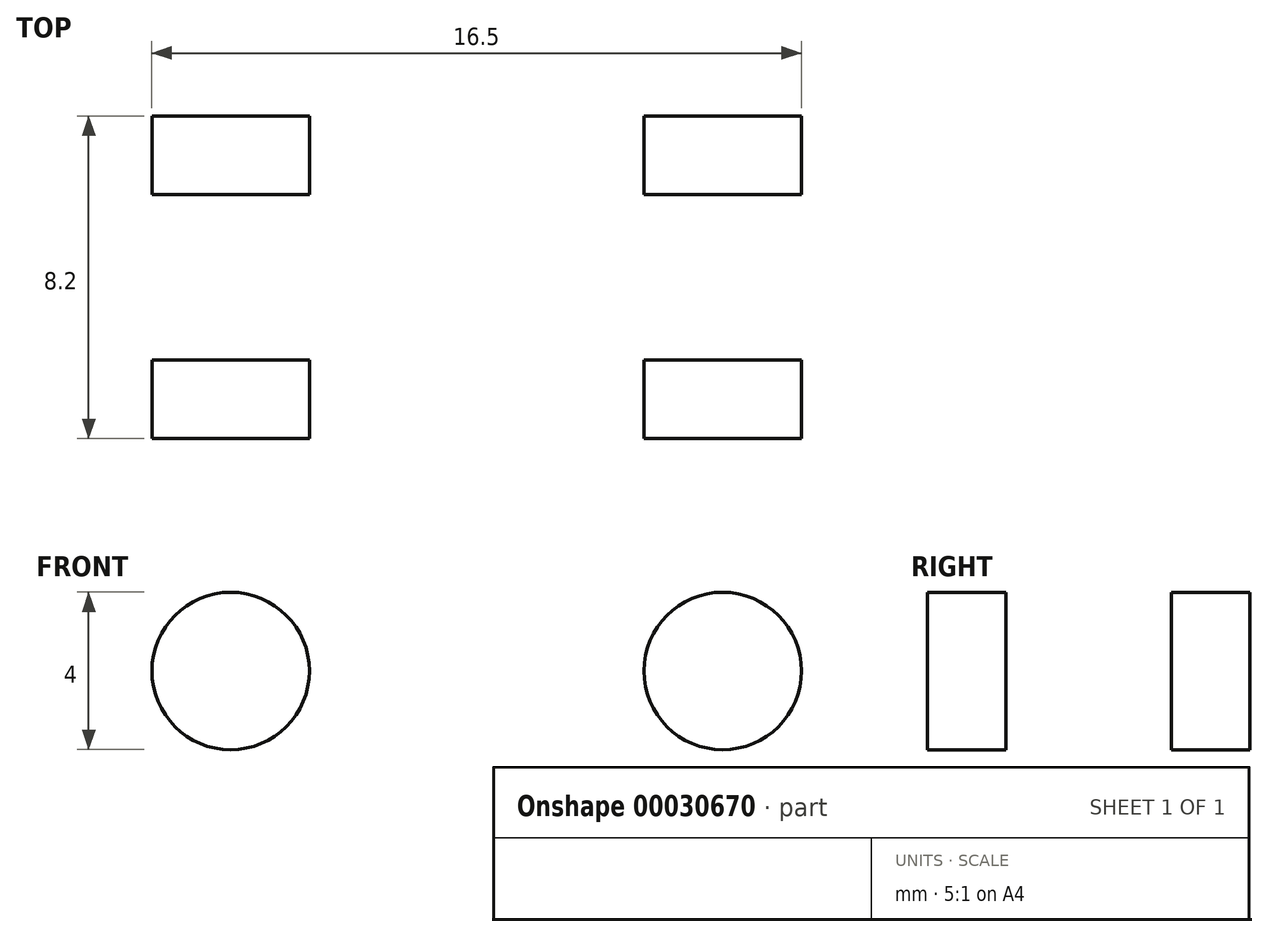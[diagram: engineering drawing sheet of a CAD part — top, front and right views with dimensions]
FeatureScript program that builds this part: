
annotation { "Feature Type Name" : "Feature", "Feature Type Description" : "" }
export const myFeature = defineFeature(function(context is Context, id is Id, definition is map)
    precondition{}
    {
        {
            var Q0;
            Q0=qCreatedBy(makeId("Front.planeOp"),FACE);
            var sketch = newSketch(context, id + "F0", { "sketchPlane" : qUnion([Q0])});
            skLineSegment(sketch, "E0", {"start": v(-39.95, 41.63) * mm, "end": v(-14.95, 41.63) * mm});
            skLineSegment(sketch, "E1", {"start": v(-39.95, 41.63) * mm, "end": v(-39.95, 11.63) * mm});
            skLineSegment(sketch, "E2", {"start": v(-39.95, 11.63) * mm, "end": v(-14.95, 11.63) * mm});
            skLineSegment(sketch, "E3", {"start": v(-14.95, 41.63) * mm, "end": v(-14.95, 11.63) * mm});
            skCircle(sketch, "E4", {"center": v(-27.45, 26.63) * mm, "radius": 2.1 * mm});
            skSolve(sketch);
        }
        {
            var Q0;
            Q0 = qSketchRegion(id + "F0", true);
            extrude(context, id + "F1", {"entities" : qUnion([Q0]), "oppositeDirection" : true, "depth" : 2 * mm});
        }
        {
            var Q0;
            Q0=makeQuery(id+"F1.opExtrude","SWEPT_FACE",FACE,{"disambiguationData":[OSD([sQuery(id+"F0.wireOp",EDGE,"E0")])]});
            var sketch = newSketch(context, id + "F2", { "sketchPlane" : qUnion([Q0])});
            skLineSegment(sketch, "E5", {"start": v(-14.95, 2) * mm, "end": v(-14.95, 6.2) * mm});
            skLineSegment(sketch, "E6", {"start": v(-14.95, 6.2) * mm, "end": v(-39.95, 6.2) * mm});
            skLineSegment(sketch, "E7", {"start": v(-39.95, 2) * mm, "end": v(-39.95, 6.2) * mm});
            skLineSegment(sketch, "E8", {"start": v(-39.95, 6.2) * mm, "end": v(-39.95, 8.2) * mm});
            skLineSegment(sketch, "E9", {"start": v(-39.95, 8.2) * mm, "end": v(-14.95, 8.2) * mm});
            skLineSegment(sketch, "E10", {"start": v(-14.95, 6.2) * mm, "end": v(-14.95, 8.2) * mm});
            skSolve(sketch);
        }
        {
            var Q0;
            Q0=makeQuery(id+"F2.imprint","IMPRINT",FACE,{"disambiguationData":[TD([[makeQuery(id+"F2.imprint","IMPRINT",EDGE,{"derivedFrom":sQuery(id+"F2.wireOp",EDGE,"E6")}),-1.0]])]});
            var Q1;
            Q1=makeQuery(id+"F2.imprint","IMPRINT",FACE,{"disambiguationData":[TD([[makeQuery(id+"F2.imprint","IMPRINT",EDGE,{"derivedFrom":sQuery(id+"F2.wireOp",EDGE,"E5")}),1.0]])]});
            var Q2;
            {var subQ0=sQuery(id+"F0.wireOp",EDGE,"E0");Q2=makeQuery(id+"F2.imprint","IMPRINT",FACE,{"disambiguationData":[TD([[makeQuery(id+"F2.imprint","IMPRINT",EDGE,{"derivedFrom":makeQuery(id+"F1.opExtrude","CAP_EDGE",EDGE,{"disambiguationData":[OSD([subQ0])],"isStart":true})}),1.0]])]});}
            extrude(context, id + "F3", {"entities" : qUnion([Q0, Q1, Q2]), "operationType" : NewBodyOperationType.ADD, "depth" : 2 * mm});
        }
        {
            var Q0;
            Q0=makeQuery(id+"F2.imprint","IMPRINT",FACE,{"disambiguationData":[TD([[makeQuery(id+"F2.imprint","IMPRINT",EDGE,{"derivedFrom":sQuery(id+"F2.wireOp",EDGE,"E6")}),-1.0]])]});
            extrude(context, id + "F4", {"entities" : qUnion([Q0]), "operationType" : NewBodyOperationType.ADD, "oppositeDirection" : true, "depth" : 30 * mm});
        }
        {
            var Q0;
            Q0=makeQuery(id+"F0.imprint","IMPRINT",FACE,{"disambiguationData":[TD([[makeQuery(id+"F0.imprint","IMPRINT",EDGE,{"derivedFrom":sQuery(id+"F0.wireOp",EDGE,"E0")}),-1.0]])]});
            var sketch = newSketch(context, id + "F5", { "sketchPlane" : qUnion([Q0])});
            skCircle(sketch, "E11.0", {"center": v(-27.45, 26.63) * mm, "radius": 2.1 * mm});
            skSolve(sketch);
        }
        {
            var Q0;
            Q0 = qSketchRegion(id + "F5", true);
            var Q1;
            {var subQ0=sQuery(id+"F2.wireOp",EDGE,"E9");Q1=makeQuery(id+"F4.boolean.opBoolean","MERGE",FACE,{"derivedFrom":[makeQuery(id+"F3.opExtrude","SWEPT_FACE",FACE,{"disambiguationData":[OSD([subQ0])]}),makeQuery(id+"F4.opExtrude","SWEPT_FACE",FACE,{"disambiguationData":[OSD([subQ0])]})]});}
            extrude(context, id + "F6", {"entities" : qUnion([Q0]), "operationType" : NewBodyOperationType.REMOVE, "endBound" : BoundingType.UP_TO_SURFACE, "oppositeDirection" : true, "endBoundEntityFace" : qUnion([Q1]), "depth" : 25 * mm});
        }
        {
            var Q0;
            Q0=qCreatedBy(makeId("Front.planeOp"),FACE);
            cPlane(context, id + "F7", {"entities" : qUnion([Q0]), "cplaneType" : CPlaneType.OFFSET, "offset" : 3.5 * mm, "oppositeDirection" : true, "width" : 150 * mm, "height" : 150 * mm});
        }
        {
            var Q0;
            Q0=qCreatedBy(id+"F7.planeOp",FACE);
            var sketch = newSketch(context, id + "F8", { "sketchPlane" : qUnion([Q0])});
            skCircle(sketch, "E12.0", {"center": v(-27.45, 26.63) * mm, "radius": 2.1 * mm});
            skCircle(sketch, "E13", {"center": v(-27.45, 26.63) * mm, "radius": 8.1 * mm});
            skSolve(sketch);
        }
        {
            var Q0;
            Q0 = qSketchRegion(id + "F8", true);
            extrude(context, id + "F9", {"entities" : qUnion([Q0]), "operationType" : NewBodyOperationType.REMOVE, "depth" : 2.5 * mm, "hasSecondDirection" : true, "secondDirectionOppositeDirection" : true, "secondDirectionDepth" : 3.5 * mm});
        }
        {
            var Q0;
            Q0=makeQuery(id+"F5.imprint","IMPRINT",FACE,{"disambiguationData":[TD([[makeQuery(id+"F5.imprint","IMPRINT",EDGE,{"derivedFrom":sQuery(id+"F5.wireOp",EDGE,"E11.0")}),-1.0]])]});
            var sketch = newSketch(context, id + "F10", { "sketchPlane" : qUnion([Q0])});
            skCircle(sketch, "E14", {"center": v(-27.45, 26.63) * mm, "radius": 4.1 * mm});
            skSolve(sketch);
        }
        {
            var Q0;
            Q0 = qSketchRegion(id + "F10", true);
            var Q1;
            Q1=makeQuery(id+"F9.boolean.opBoolean","COPY",FACE,{"derivedFrom":makeQuery(id+"F9.opExtrude","CAP_FACE",FACE,{"disambiguationData":[OSD([sQuery(id+"F8.wireOp",EDGE,"E12.0"),sQuery(id+"F8.wireOp",EDGE,"E13")])],"isStart":false})});
            extrude(context, id + "F11", {"entities" : qUnion([Q0]), "operationType" : NewBodyOperationType.REMOVE, "endBound" : BoundingType.UP_TO_SURFACE, "oppositeDirection" : true, "endBoundEntityFace" : qUnion([Q1]), "depth" : 25 * mm});
        }
        {
            var Q0;
            {var subQ0=sQuery(id+"F2.wireOp",EDGE,"E9");Q0=makeQuery(id+"F4.boolean.opBoolean","MERGE",FACE,{"derivedFrom":[makeQuery(id+"F3.opExtrude","SWEPT_FACE",FACE,{"disambiguationData":[OSD([subQ0])]}),makeQuery(id+"F4.opExtrude","SWEPT_FACE",FACE,{"disambiguationData":[OSD([subQ0])]})]});}
            var sketch = newSketch(context, id + "F12", { "sketchPlane" : qUnion([Q0])});
            skCircle(sketch, "E15", {"center": v(21.2, 15.63) * mm, "radius": 2 * mm});
            skCircle(sketch, "E16", {"center": v(33.7, 15.63) * mm, "radius": 2 * mm});
            skCircle(sketch, "E17.MirrorC", {"center": v(21.2, 37.63) * mm, "radius": 2 * mm});
            skCircle(sketch, "E18.MirrorC", {"center": v(33.7, 37.63) * mm, "radius": 2 * mm});
            skSolve(sketch);
        }
        {
            var Q0;
            Q0=makeQuery(id+"F12.imprint","IMPRINT",FACE,{"disambiguationData":[TD([[makeQuery(id+"F12.imprint","IMPRINT",EDGE,{"derivedFrom":sQuery(id+"F12.wireOp",EDGE,"E17.MirrorC")}),-1.0]])]});
            var Q1;
            Q1=makeQuery(id+"F12.imprint","IMPRINT",FACE,{"disambiguationData":[TD([[makeQuery(id+"F12.imprint","IMPRINT",EDGE,{"derivedFrom":sQuery(id+"F12.wireOp",EDGE,"E18.MirrorC")}),-1.0]])]});
            var Q2;
            Q2=makeQuery(id+"F12.imprint","IMPRINT",FACE,{"disambiguationData":[TD([[makeQuery(id+"F12.imprint","IMPRINT",EDGE,{"derivedFrom":sQuery(id+"F12.wireOp",EDGE,"E15")}),1.0]])]});
            var Q3;
            Q3=makeQuery(id+"F12.imprint","IMPRINT",FACE,{"disambiguationData":[TD([[makeQuery(id+"F12.imprint","IMPRINT",EDGE,{"derivedFrom":sQuery(id+"F12.wireOp",EDGE,"E16")}),1.0]])]});
            var Q4;
            Q4=sQuery(id+"F12.wireOp",EDGE,"E17.MirrorC");
            var Q5;
            Q5=sQuery(id+"F12.wireOp",EDGE,"E18.MirrorC");
            var Q6;
            Q6=sQuery(id+"F12.wireOp",EDGE,"E15");
            var Q7;
            Q7=sQuery(id+"F12.wireOp",EDGE,"E16");
            var Q8;
            {var subQ0=sQuery(id+"F0.wireOp",EDGE,"E0");Q8=makeQuery(id+"F3.boolean.opBoolean","MERGE",FACE,{"derivedFrom":[makeQuery(id+"F1.opExtrude","CAP_FACE",FACE,{"disambiguationData":[OSD([subQ0,sQuery(id+"F0.wireOp",EDGE,"E1"),sQuery(id+"F0.wireOp",EDGE,"E2"),sQuery(id+"F0.wireOp",EDGE,"E3"),sQuery(id+"F0.wireOp",EDGE,"E4")])],"isStart":true}),makeQuery(id+"F3.opExtrude","SWEPT_FACE",FACE,{"disambiguationData":[OSD([subQ0])]})]});}
            extrude(context, id + "F13", {"entities" : qUnion([Q0, Q1, Q2, Q3]), "operationType" : NewBodyOperationType.REMOVE, "surfaceEntities" : qUnion([Q4, Q5, Q6, Q7]), "endBound" : BoundingType.UP_TO_SURFACE, "oppositeDirection" : true, "endBoundEntityFace" : qUnion([Q8]), "depth" : 25 * mm});
        }
    });
